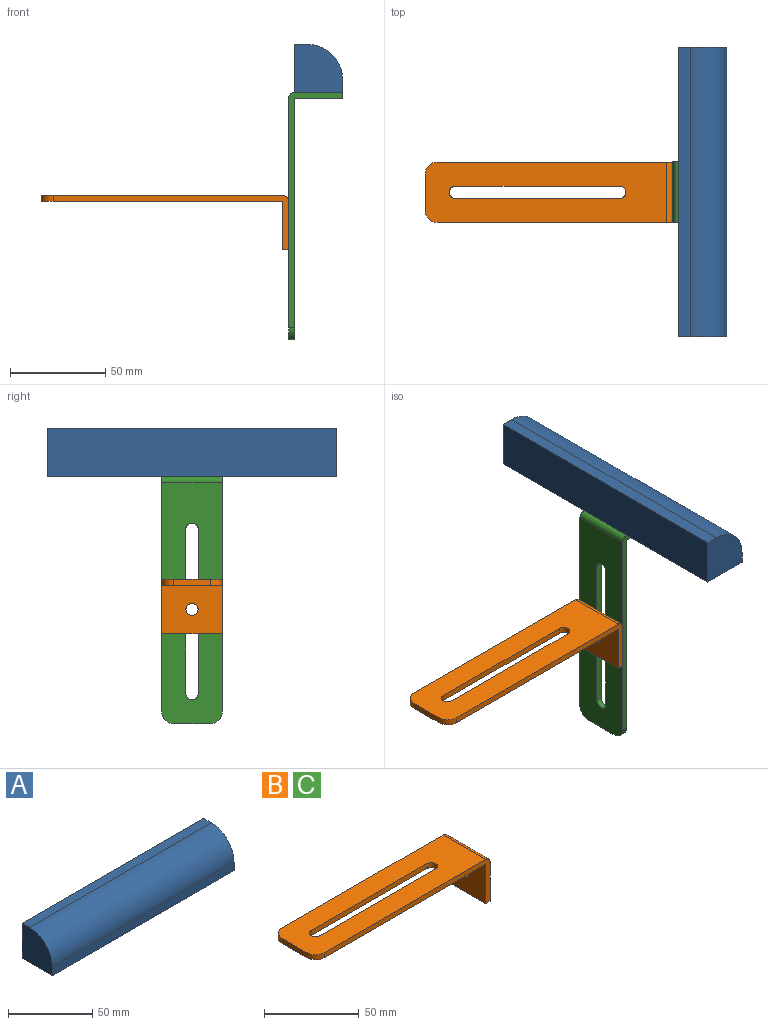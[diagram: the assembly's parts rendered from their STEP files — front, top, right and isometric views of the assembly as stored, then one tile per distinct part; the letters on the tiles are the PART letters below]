
ASSEMBLY  parts=3 mates=2
PART A: 9 faces, bbox 152.4x25.4x25.4 mm
  f0: plane 152.4x25.4mm, normal (0,1,0), area 3871mm2, adj f1,f4,f5,f6
  f1: plane 152.4x6.35mm, normal (0,0,1), area 967.7mm2, adj f0,f2,f5,f6
  f2: cylinder r=19.05mm len=152.4mm, axis (-1,0,0), area 4560.4mm2, adj f1,f3,f5,f6
  f3: plane 152.4x6.35mm, normal (0,-1,0), area 967.7mm2, adj f2,f4,f5,f6
  f4: plane 152.4x25.4mm, normal (0,0,-1), area 3837.5mm2, adj f0,f3,f5,f6,f7
  f5: plane 25.4x25.4mm, normal (1,0,0), area 567.3mm2, adj f0,f1,f2,f3,f4
  f6: plane 25.4x25.4mm, normal (-1,0,0), area 567.3mm2, adj f0,f1,f2,f3,f4
  f7: cylinder r=3.26mm len=19.05mm, axis (0,0,-1), area 390.7mm2, adj f4,f8
  f8: plane 6.53x6.53mm, normal (0,0,-1), area 33.5mm2, adj f7
PART B: 16 faces, bbox 130.2x31.8x28.6 mm
  f0: plane 31.75x25.4mm, normal (-1,0,0), area 774.8mm2, adj f1,f3,f4,f6,f15
  f1: plane 123.83x28.58mm, normal (0,-1,0), area 471.6mm2, adj f0,f2,f4,f5,f7,f14,f15
  f2: plane 31.75x25.4mm, normal (1,0,0), area 774.8mm2, adj f1,f3,f4,f5,f6
  f3: plane 123.83x28.58mm, normal (0,1,0), area 471.6mm2, adj f0,f2,f4,f5,f8,f14,f15
  f4: plane 31.75x3.18mm, normal (0,0,-1), area 100.8mm2, adj f0,f1,f2,f3
  f5: cylinder r=3.17mm len=31.75mm, axis (0,1,0), area 158.3mm2, adj f1,f2,f3,f14
  f6: cylinder r=3.17mm len=6.35mm, axis (-1,0,0), area 63.3mm2, adj f0,f2
  f7: cylinder r=6.35mm len=6.35mm, axis (0,0,1), area 31.7mm2, adj f1,f13,f14,f15
  f8: cylinder r=6.35mm len=6.35mm, axis (0,0,1), area 31.7mm2, adj f3,f13,f14,f15
  f9: cylinder r=3.26mm len=6.53mm, axis (0,0,1), area 32.6mm2, adj f10,f12,f14,f15
  f10: plane 86.32x3.18mm, normal (0,1,0), area 274.1mm2, adj f9,f11,f14,f15
  f11: cylinder r=3.26mm len=6.53mm, axis (0,0,1), area 33mm2, adj f10,f12,f14,f15
  f12: plane 86.19x3.18mm, normal (0,-1,0), area 273.7mm2, adj f9,f11,f14,f15
  f13: plane 19.05x3.18mm, normal (-1,0,0), area 60.5mm2, adj f7,f8,f14,f15
  f14: plane 127x31.75mm, normal (0,0,1), area 3418.1mm2, adj f1,f3,f5,f7,f8,f9,f10,f11
  f15: plane 127x31.75mm, normal (0,0,-1), area 3418.1mm2, adj f0,f1,f3,f7,f8,f9,f10,f11
PART C: same geometry as B
PLACE A rot(axis=(0,0,1),90deg) t=(140.83,-58.73,201.75)mm
PLACE B rot(axis=(0,0,-1),0deg) t=(70.6,8.89,148.73)mm
PLACE C rot(axis=(0,-1,0),90deg) t=(127.07,8.89,152.74)mm
MATE pin_slot A.f7 <-> C.f6  axis (0,0,-1) through (139.77,17.47,206.04)mm
MATE pin_slot C.f11 <-> B.f6  axis (-1,0,0) through (123.89,17.47,91.83)mm
